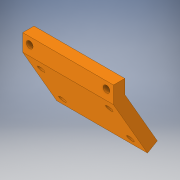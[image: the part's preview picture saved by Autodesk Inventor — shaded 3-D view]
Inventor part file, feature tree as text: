
AUTODESK INVENTOR PART (.ipt)
format: ipt  version: 2019 (Build 230136000, 136)  size: 138,240 bytes
history: native  units: in
note: dims shown in document units (in); Inventor stores cm internally (conversion verified against a paired STEP export)
features: sketch x4, extrude x2, hole x2, plane x1, projected_geometry x1
ambient origin geometry x8: Origin, YZ Plane, XZ Plane, XY Plane, X Axis, Y Axis, Z Axis, Center Point
bodies: Solid1 (feature_tree)
feature tree (10):
  extrude  "Extrusion1"  Depth=0.25in
  plane  "Work Plane1"
  extrude  "Extrusion2"  TaperAngle=30.0deg  [1 undecoded]
  hole  "Hole1"  [1 undecoded]
  hole  "Hole2"  [1 undecoded]
  sketch  "Sketch1"  dims[d0=0.375in d1=0.25in]
  sketch  "Sketch2"  dims[d2=2.0in d3=0.0in d4=30.0deg]
  sketch  "Sketch3"  dims[d5=0.25in d6=1.5in d7=0.0in]
  sketch  "Sketch4"  dims[d8=0.154in d9=0.308in d10=0.154in d11=0.154in d12=0.154in d13=0.15in d14=0.75in d15=0.375in d16=0.25in d17=0.5635in d18=1.0in d19=0.8108in d20=0.25in d21=0.25in d22=0.25in d23=0.25in d24=0.25in d25=0.25in d26=0.25in d27=0.25in d28=0.15in d29=0.75in d30=0.375in d31=0.25in d32=0.5635in d33=1.0in d34=0.8108in]
  projected_geometry  "Projected Loop1"
note: 3 required parameter values undecoded (feature->parameter linkage not recoverable at this tier; creation-order binding heuristic only, values carry confidence <= 0.55)
